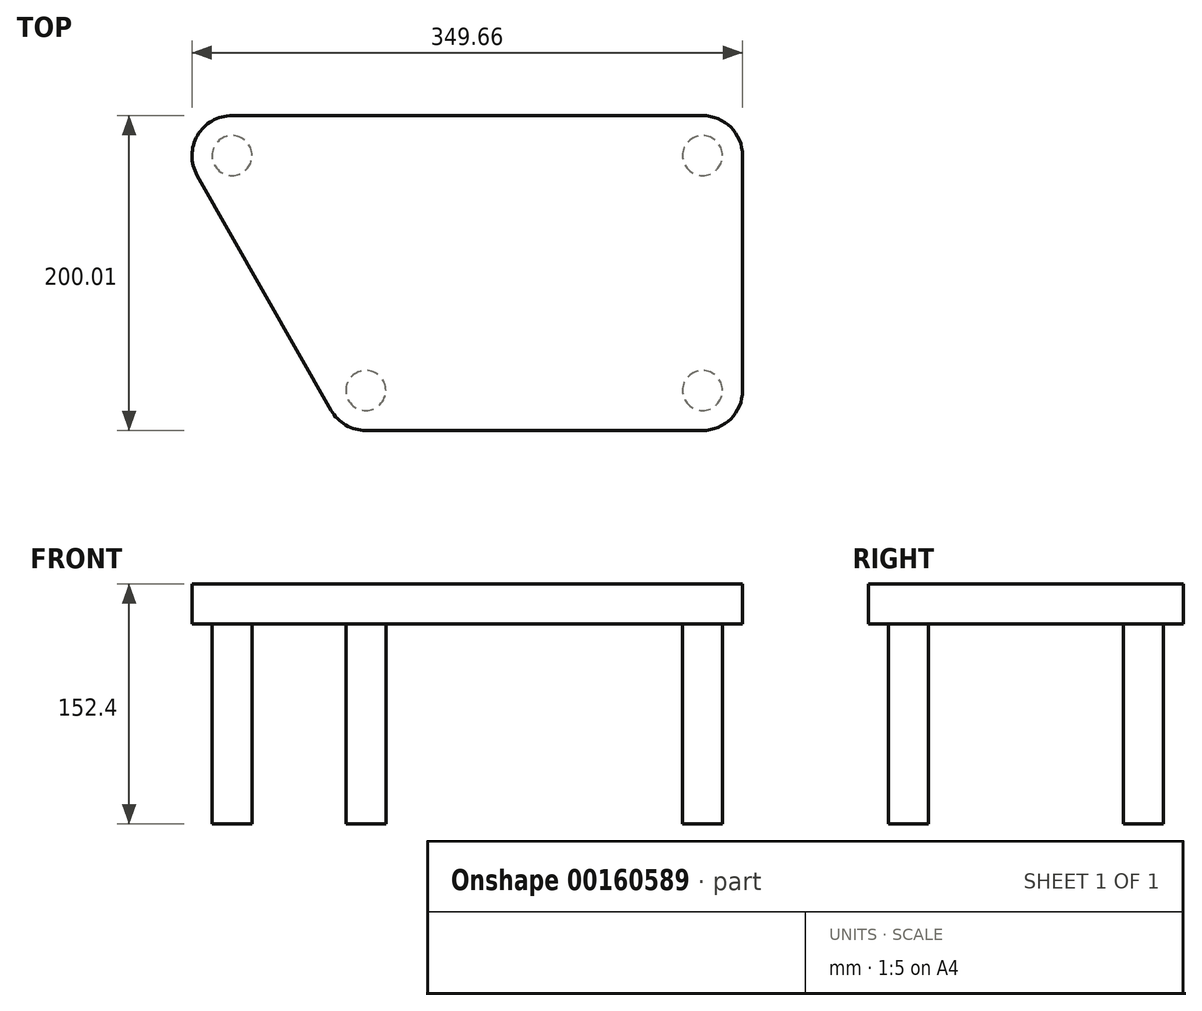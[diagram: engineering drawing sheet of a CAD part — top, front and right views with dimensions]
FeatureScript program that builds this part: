
annotation { "Feature Type Name" : "Feature", "Feature Type Description" : "" }
export const myFeature = defineFeature(function(context is Context, id is Id, definition is map)
    precondition{}
    {
        {
            var Q0;
            Q0=qCreatedBy(makeId("Top.planeOp"),FACE);
            var sketch = newSketch(context, id + "F0", { "sketchPlane" : qUnion([Q0])});
            skLineSegment(sketch, "E0", {"start": v(-134.46, 109.23) * mm, "end": v(164.4, 109.23) * mm});
            skLineSegment(sketch, "E1", {"start": v(189.8, 83.83) * mm, "end": v(189.8, -65.38) * mm});
            skLineSegment(sketch, "E2", {"start": v(164.4, -90.78) * mm, "end": v(-49.44, -90.78) * mm});
            skLineSegment(sketch, "E3", {"start": v(-71.5, -77.95) * mm, "end": v(-156.53, 71.26) * mm});
            skPoint(sketch, "E4.visualSharp", {"position": v(-64.2, -90.78) * mm});
            skArc(sketch, "E4.filletArc", {"start": v(-71.5, -77.95) * mm, "mid": v(-62.2, -87.34) * mm, "end": v(-49.44, -90.78) * mm});
            skPoint(sketch, "E5.visualSharp", {"position": v(189.8, -90.78) * mm});
            skArc(sketch, "E5.filletArc", {"start": v(164.4, -90.78) * mm, "mid": v(182.36, -83.34) * mm, "end": v(189.8, -65.38) * mm});
            skPoint(sketch, "E6.visualSharp", {"position": v(189.8, 109.23) * mm});
            skArc(sketch, "E6.filletArc", {"start": v(189.8, 83.83) * mm, "mid": v(182.36, 101.8) * mm, "end": v(164.4, 109.23) * mm});
            skPoint(sketch, "E7.visualSharp", {"position": v(-178.16, 109.23) * mm});
            skArc(sketch, "E7.filletArc", {"start": v(-134.46, 109.23) * mm, "mid": v(-156.42, 96.6) * mm, "end": v(-156.53, 71.26) * mm});
            skCircle(sketch, "E8", {"center": v(-134.46, 83.83) * mm, "radius": 12.7 * mm});
            skCircle(sketch, "E9", {"center": v(164.4, 83.83) * mm, "radius": 12.7 * mm});
            skCircle(sketch, "E10", {"center": v(164.4, -65.38) * mm, "radius": 12.7 * mm});
            skCircle(sketch, "E11", {"center": v(-49.44, -65.38) * mm, "radius": 12.7 * mm});
            skSolve(sketch);
        }
        {
            var Q0;
            Q0=makeQuery(id+"F0.imprint","IMPRINT",FACE,{"disambiguationData":[TD([[makeQuery(id+"F0.imprint","IMPRINT",EDGE,{"derivedFrom":sQuery(id+"F0.wireOp",EDGE,"E8")}),1.0]])]});
            var Q1;
            Q1=sQuery(id+"F0.wireOp",EDGE,"E8");
            extrude(context, id + "F1", {"entities" : qUnion([Q0]), "surfaceEntities" : qUnion([Q1]), "oppositeDirection" : true, "depth" : 127 * mm});
        }
        {
            var Q0;
            Q0=makeQuery(id+"F0.imprint","IMPRINT",FACE,{"disambiguationData":[TD([[makeQuery(id+"F0.imprint","IMPRINT",EDGE,{"derivedFrom":sQuery(id+"F0.wireOp",EDGE,"E11")}),1.0]])]});
            extrude(context, id + "F2", {"entities" : qUnion([Q0]), "oppositeDirection" : true, "depth" : 127 * mm});
        }
        {
            var Q0;
            Q0=makeQuery(id+"F0.imprint","IMPRINT",FACE,{"disambiguationData":[TD([[makeQuery(id+"F0.imprint","IMPRINT",EDGE,{"derivedFrom":sQuery(id+"F0.wireOp",EDGE,"E10")}),1.0]])]});
            var Q1;
            Q1=sQuery(id+"F0.wireOp",EDGE,"E10");
            extrude(context, id + "F3", {"entities" : qUnion([Q0]), "surfaceEntities" : qUnion([Q1]), "oppositeDirection" : true, "depth" : 127 * mm});
        }
        {
            var Q0;
            Q0=makeQuery(id+"F0.imprint","IMPRINT",FACE,{"disambiguationData":[TD([[makeQuery(id+"F0.imprint","IMPRINT",EDGE,{"derivedFrom":sQuery(id+"F0.wireOp",EDGE,"E9")}),1.0]])]});
            var Q1;
            Q1=sQuery(id+"F0.wireOp",EDGE,"E9");
            extrude(context, id + "F4", {"entities" : qUnion([Q0]), "surfaceEntities" : qUnion([Q1]), "oppositeDirection" : true, "depth" : 127 * mm});
        }
        {
            var Q0;
            Q0=makeQuery(id+"F0.imprint","IMPRINT",FACE,{"disambiguationData":[TD([[makeQuery(id+"F0.imprint","IMPRINT",EDGE,{"derivedFrom":sQuery(id+"F0.wireOp",EDGE,"E0")}),-1.0]])]});
            var Q1;
            Q1=makeQuery(id+"F0.imprint","IMPRINT",FACE,{"disambiguationData":[TD([[makeQuery(id+"F0.imprint","IMPRINT",EDGE,{"derivedFrom":sQuery(id+"F0.wireOp",EDGE,"E11")}),1.0]])]});
            var Q2;
            Q2=makeQuery(id+"F0.imprint","IMPRINT",FACE,{"disambiguationData":[TD([[makeQuery(id+"F0.imprint","IMPRINT",EDGE,{"derivedFrom":sQuery(id+"F0.wireOp",EDGE,"E8")}),1.0]])]});
            var Q3;
            Q3=makeQuery(id+"F0.imprint","IMPRINT",FACE,{"disambiguationData":[TD([[makeQuery(id+"F0.imprint","IMPRINT",EDGE,{"derivedFrom":sQuery(id+"F0.wireOp",EDGE,"E9")}),1.0]])]});
            var Q4;
            Q4=makeQuery(id+"F0.imprint","IMPRINT",FACE,{"disambiguationData":[TD([[makeQuery(id+"F0.imprint","IMPRINT",EDGE,{"derivedFrom":sQuery(id+"F0.wireOp",EDGE,"E10")}),1.0]])]});
            extrude(context, id + "F5", {"entities" : qUnion([Q0, Q1, Q2, Q3, Q4]), "depth" : 25.4 * mm});
        }
    });
